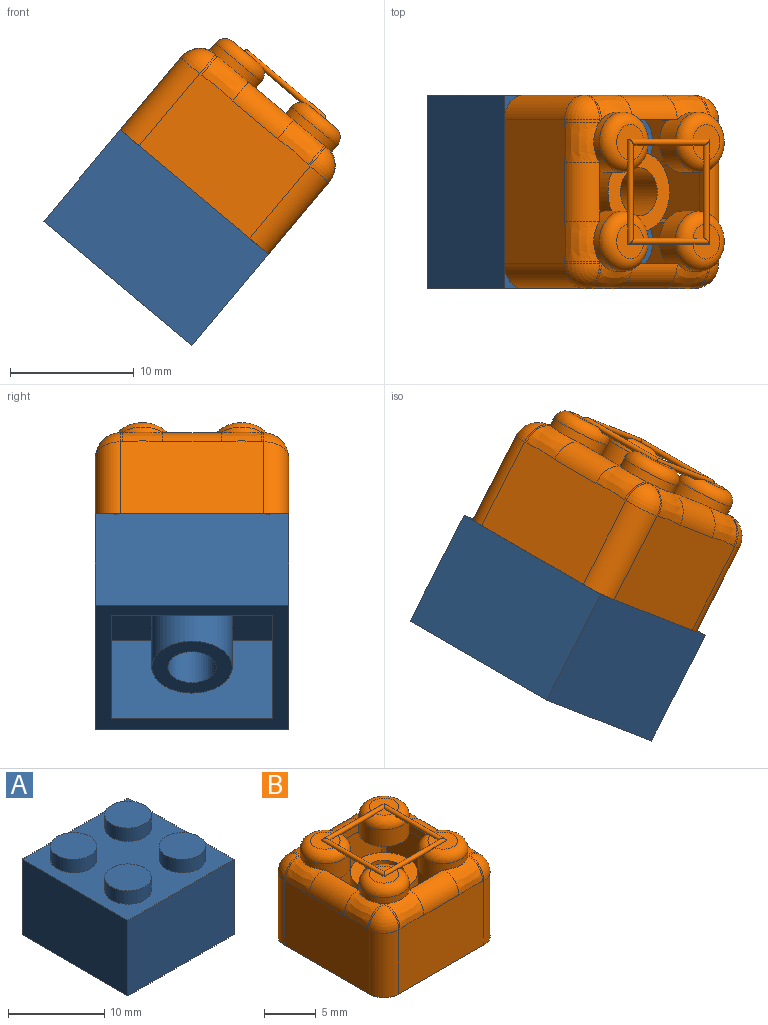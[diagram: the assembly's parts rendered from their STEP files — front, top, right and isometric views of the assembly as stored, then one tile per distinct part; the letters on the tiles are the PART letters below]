
ASSEMBLY  parts=2 mates=1
PART A: 23 faces, bbox 15.6x15.6x11.3 mm
  f0: plane 15.6x9.6mm, normal (1,0,0), area 149.8mm2, adj f1,f3,f4,f5
  f1: plane 15.6x9.6mm, normal (0,1,0), area 149.8mm2, adj f0,f2,f4,f5
  f2: plane 15.6x9.6mm, normal (-1,0,0), area 149.8mm2, adj f1,f3,f4,f5
  f3: plane 15.6x9.6mm, normal (0,-1,0), area 149.8mm2, adj f0,f2,f4,f5
  f4: plane 15.6x15.6mm, normal (0,0,1), area 169.5mm2, adj f0,f1,f2,f3,f11,f13,f15,f17
  f5: plane 15.6x15.6mm, normal (0,0,-1), area 74.4mm2, adj f0,f1,f2,f3,f6,f7,f8,f9
  f6: plane 13x8.3mm, normal (-1,0,0), area 107.9mm2, adj f5,f7,f9,f10
  f7: plane 13x8.3mm, normal (0,-1,0), area 107.9mm2, adj f5,f6,f8,f10
  f8: plane 13x8.3mm, normal (1,0,0), area 107.9mm2, adj f5,f7,f9,f10
  f9: plane 13x8.3mm, normal (0,1,0), area 107.9mm2, adj f5,f6,f8,f10
  f10: plane 13x13mm, normal (0,0,-1), area 135.8mm2, adj f6,f7,f8,f9,f20
  f11: cylinder r=2.43mm len=4.85mm, axis (0,0,-1), area 25.9mm2, adj f4,f12
  f12: plane 4.85x4.85mm, normal (0,0,1), area 18.5mm2, adj f11
  f13: cylinder r=2.43mm len=4.85mm, axis (0,0,-1), area 25.9mm2, adj f4,f14
  f14: plane 4.85x4.85mm, normal (0,0,1), area 18.5mm2, adj f13
  f15: cylinder r=2.43mm len=4.85mm, axis (0,0,-1), area 25.9mm2, adj f4,f16
  f16: plane 4.85x4.85mm, normal (0,0,1), area 18.5mm2, adj f15
  f17: cylinder r=2.43mm len=4.85mm, axis (0,0,-1), area 25.9mm2, adj f4,f18
  f18: plane 4.85x4.85mm, normal (0,0,1), area 18.5mm2, adj f17
  f19: plane 6.5x6.5mm, normal (0,0,-1), area 21.2mm2, adj f20,f22
  f20: cylinder r=3.25mm len=8.3mm, axis (0,0,1), area 169.5mm2, adj f10,f19
  f21: plane 3.9x3.9mm, normal (0,0,-1), area 11.9mm2, adj f22
  f22: cylinder r=1.95mm len=8.3mm, axis (0,0,1), area 101.7mm2, adj f19,f21
PART B: 70 faces, bbox 15.6x15.6x11.6 mm
  f0: plane 13x13mm, normal (0,0,-1), area 97.2mm2, adj f1,f16,f17,f18,f19,f20,f22,f24
  f1: cylinder r=3.25mm len=8.3mm, axis (0,0,1), area 156.5mm2, adj f0,f20,f22,f24,f26,f28,f69
  f2: cylinder r=1.95mm len=7.6mm, axis (0,0,1), area 93.1mm2, adj f28,f69
  f3: plane 2.83x2.83mm, normal (0,0,1), area 4mm2, adj f60,f62,f64
  f4: plane 2.83x2.83mm, normal (0,0,1), area 4mm2, adj f59,f61,f62
  f5: plane 2.83x2.83mm, normal (0,0,1), area 4mm2, adj f58,f63,f64
  f6: plane 2.83x2.83mm, normal (0,0,1), area 4mm2, adj f57,f61,f63
  f7: plane 0.18x0.18mm, normal (0,0,1), area 0mm2, adj f20,f41,f46
  f8: plane 0.18x0.18mm, normal (0,0,1), area 0mm2, adj f22,f53,f54
  f9: plane 0.18x0.18mm, normal (0,0,1), area 0mm2, adj f24,f31,f32
  f10: plane 11.6x7.7mm, normal (1,0,0), area 88.5mm2, adj f15,f39,f45,f47,f49,f51,f53,f56
  f11: plane 11.6x7.7mm, normal (0,1,0), area 88.5mm2, adj f15,f42,f46,f48,f50,f52,f54,f56
  f12: plane 11.6x7.7mm, normal (-1,0,0), area 88.5mm2, adj f15,f29,f32,f34,f36,f38,f41,f42
  f13: plane 11.6x7.7mm, normal (0,-1,0), area 88.5mm2, adj f15,f29,f31,f33,f35,f37,f39,f40
  f14: plane 0.18x0.18mm, normal (0,0,1), area 0mm2, adj f26,f40,f45
  f15: plane 15.6x15.6mm, normal (0,0,-1), area 70.9mm2, adj f10,f11,f12,f13,f16,f17,f18,f19
  f16: plane 13x8.3mm, normal (-1,0,0), area 107.9mm2, adj f0,f15,f17,f19
  f17: plane 13x8.3mm, normal (0,-1,0), area 107.9mm2, adj f0,f15,f16,f18
  f18: plane 13x8.3mm, normal (1,0,0), area 107.9mm2, adj f0,f15,f17,f19
  f19: plane 13x8.3mm, normal (0,1,0), area 107.9mm2, adj f0,f15,f16,f18
  f20: cylinder r=2.43mm len=4.85mm, axis (0,0,-1), area 21.2mm2, adj f0,f1,f7,f38,f48,f60,f65,f68
  f21: plane 1.16x1.16mm, normal (0,0,1), area 1mm2, adj f60,f62,f64
  f22: cylinder r=2.43mm len=4.85mm, axis (0,0,-1), area 21.2mm2, adj f0,f1,f8,f51,f52,f59,f67,f68
  f23: plane 1.16x1.16mm, normal (0,0,1), area 1mm2, adj f59,f61,f62
  f24: cylinder r=2.43mm len=4.85mm, axis (0,0,-1), area 21.2mm2, adj f0,f1,f9,f33,f34,f58,f65,f66
  f25: plane 1.16x1.16mm, normal (0,0,1), area 1mm2, adj f58,f63,f64
  f26: cylinder r=2.43mm len=4.85mm, axis (0,0,-1), area 21.2mm2, adj f0,f1,f14,f37,f47,f57,f66,f67
  f27: plane 1.16x1.16mm, normal (0,0,1), area 1mm2, adj f57,f61,f63
  f28: plane 6.5x6.5mm, normal (0,0,-1), area 21.2mm2, adj f1,f2
  f29: cylinder r=2mm len=7.6mm, axis (0,0,-1), area 23.9mm2, adj f12,f13,f15,f30
  f30: sphere r=2mm, area 6.3mm2, adj f29,f31,f32
  f31: cylinder r=2mm len=2mm, axis (-1,0,0), area 0.5mm2, adj f9,f13,f30,f33
  f32: cylinder r=2mm len=2mm, axis (0,1,0), area 0.5mm2, adj f9,f12,f30,f34
  f33: bspline ~3.25x2mm, area 8.8mm2, adj f13,f24,f31,f35
  f34: bspline ~3.25x2mm, area 8.8mm2, adj f12,f24,f32,f36
  f35: cylinder r=2mm len=4.75mm, axis (-1,0,0), area 14.9mm2, adj f13,f33,f37,f66
  f36: cylinder r=2mm len=4.75mm, axis (0,1,0), area 14.9mm2, adj f12,f34,f38,f65
  f37: bspline ~3.25x2mm, area 8.8mm2, adj f13,f26,f35,f40
  f38: bspline ~3.25x2mm, area 8.8mm2, adj f12,f20,f36,f41
  f39: cylinder r=2mm len=7.6mm, axis (0,0,1), area 23.9mm2, adj f10,f13,f15,f43
  f40: cylinder r=2mm len=2mm, axis (-1,0,0), area 0.5mm2, adj f13,f14,f37,f43
  f41: cylinder r=2mm len=2mm, axis (0,1,0), area 0.5mm2, adj f7,f12,f38,f44
  f42: cylinder r=2mm len=7.6mm, axis (0,0,1), area 23.9mm2, adj f11,f12,f15,f44
  f43: sphere r=2mm, area 6.3mm2, adj f39,f40,f45
  f44: sphere r=2mm, area 6.3mm2, adj f41,f42,f46
  f45: cylinder r=2mm len=2mm, axis (0,-1,0), area 0.5mm2, adj f10,f14,f43,f47
  f46: cylinder r=2mm len=2mm, axis (1,0,0), area 0.5mm2, adj f7,f11,f44,f48
  f47: bspline ~3.25x2mm, area 8.8mm2, adj f10,f26,f45,f49
  f48: bspline ~3.25x2mm, area 8.8mm2, adj f11,f20,f46,f50
  f49: cylinder r=2mm len=4.75mm, axis (0,-1,0), area 14.9mm2, adj f10,f47,f51,f67
  f50: cylinder r=2mm len=4.75mm, axis (1,0,0), area 14.9mm2, adj f11,f48,f52,f68
  f51: bspline ~3.25x2mm, area 8.8mm2, adj f10,f22,f49,f53
  f52: bspline ~3.25x2mm, area 8.8mm2, adj f11,f22,f50,f54
  f53: cylinder r=2mm len=2mm, axis (0,-1,0), area 0.5mm2, adj f8,f10,f51,f55
  f54: cylinder r=2mm len=2mm, axis (1,0,0), area 0.5mm2, adj f8,f11,f52,f55
  f55: sphere r=2mm, area 6.3mm2, adj f53,f54,f56
  f56: cylinder r=2mm len=7.6mm, axis (0,0,-1), area 23.9mm2, adj f10,f11,f15,f55
  f57: torus R=1.43mm, axis (0,0,1), area 19.7mm2, adj f6,f26,f27,f61,f63
  f58: torus R=1.43mm, axis (0,0,1), area 19.7mm2, adj f5,f24,f25,f63,f64
  f59: torus R=1.43mm, axis (0,0,1), area 19.7mm2, adj f4,f22,f23,f61,f62
  f60: torus R=1.43mm, axis (0,0,1), area 19.7mm2, adj f3,f20,f21,f62,f64
  f61: cylinder r=0.25mm len=8.49mm, axis (0,1,0), area 9.5mm2, adj f4,f6,f23,f27,f57,f59,f62,f63
  f62: cylinder r=0.25mm len=8.49mm, axis (-1,0,0), area 9.5mm2, adj f3,f4,f21,f23,f59,f60,f61,f64
  f63: cylinder r=0.25mm len=8.49mm, axis (1,0,0), area 9.5mm2, adj f5,f6,f25,f27,f57,f58,f61,f64
  f64: cylinder r=0.25mm len=8.49mm, axis (0,-1,0), area 9.5mm2, adj f3,f5,f21,f25,f58,f60,f62,f63
  f65: plane 4.75x1.3mm, normal (1,0,0), area 6.2mm2, adj f0,f20,f24,f36
  f66: plane 4.75x1.3mm, normal (0,1,0), area 6.2mm2, adj f0,f24,f26,f35
  f67: plane 4.75x1.3mm, normal (-1,0,0), area 6.2mm2, adj f0,f22,f26,f49
  f68: plane 4.75x1.3mm, normal (0,-1,0), area 6.2mm2, adj f0,f20,f22,f50
  f69: plane 6.5x6.5mm, normal (0,0,1), area 21.2mm2, adj f1,f2,f20,f22,f24,f26
PLACE A rot(axis=(0,1,0),40deg) t=(-52.98,-31.2,-8.78)mm
PLACE B rot(axis=(0.32,0.32,0.89),96.7deg) t=(-46.81,-31.2,-1.42)mm
MATE slider A.f20 <-> B.f1  axis (0.64,0,0.77) through (-46.81,-31.2,-1.42)mm
